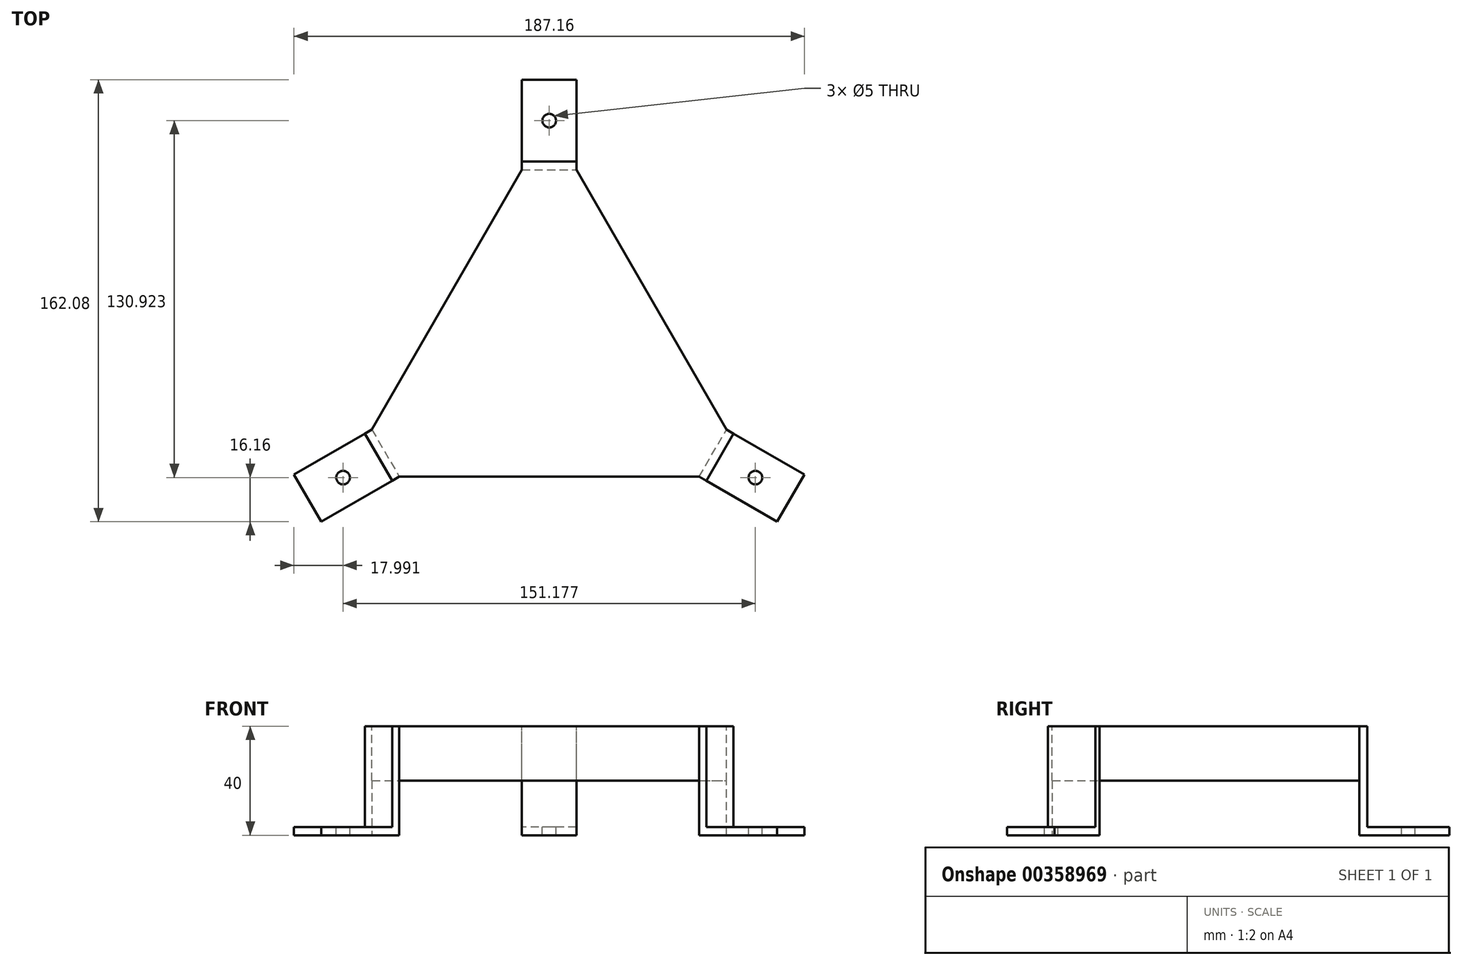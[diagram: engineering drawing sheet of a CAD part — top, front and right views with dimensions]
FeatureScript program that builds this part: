
annotation { "Feature Type Name" : "Feature", "Feature Type Description" : "" }
export const myFeature = defineFeature(function(context is Context, id is Id, definition is map)
    precondition{}
    {
        {
            var Q0;
            Q0=qCreatedBy(makeId("Top.planeOp"),FACE);
            var sketch = newSketch(context, id + "F0", { "sketchPlane" : qUnion([Q0])});
            skLineSegment(sketch, "E0", {"start": v(150, 0) * mm, "end": v(0, 0) * mm});
            skLineSegment(sketch, "E1", {"start": v(0, 0) * mm, "end": v(75, 129.9) * mm});
            skLineSegment(sketch, "E2", {"start": v(75, 129.9) * mm, "end": v(150, 0) * mm});
            skSolve(sketch);
        }
        {
            var Q0;
            Q0=makeQuery(id+"F0.imprint","IMPRINT",FACE,{"disambiguationData":[TD([[makeQuery(id+"F0.imprint","IMPRINT",EDGE,{"derivedFrom":sQuery(id+"F0.wireOp",EDGE,"E0")}),-1.0]])]});
            extrude(context, id + "F1", {"entities" : qUnion([Q0]), "depth" : 20 * mm});
        }
        {
            var Q0;
            Q0=makeQuery(id+"F1.opExtrude","CAP_FACE",FACE,{"disambiguationData":[OSD([sQuery(id+"F0.wireOp",EDGE,"E0"),sQuery(id+"F0.wireOp",EDGE,"E1"),sQuery(id+"F0.wireOp",EDGE,"E2")])],"isStart":false});
            var sketch = newSketch(context, id + "F2", { "sketchPlane" : qUnion([Q0])});
            skLineSegment(sketch, "E3", {"start": v(10, 17.32) * mm, "end": v(20, 0) * mm});
            skLineSegment(sketch, "E4", {"start": v(20, 0) * mm, "end": v(0, 0) * mm});
            skLineSegment(sketch, "E5", {"start": v(0, 0) * mm, "end": v(10, 17.32) * mm});
            skLineSegment(sketch, "E6", {"start": v(75, 129.9) * mm, "end": v(65, 112.58) * mm});
            skLineSegment(sketch, "E7", {"start": v(65, 112.58) * mm, "end": v(85, 112.58) * mm});
            skLineSegment(sketch, "E8", {"start": v(85, 112.58) * mm, "end": v(75, 129.9) * mm});
            skLineSegment(sketch, "E9", {"start": v(150, 0) * mm, "end": v(130, 0) * mm});
            skLineSegment(sketch, "E10", {"start": v(130, 0) * mm, "end": v(140, 17.32) * mm});
            skLineSegment(sketch, "E11", {"start": v(140, 17.32) * mm, "end": v(150, 0) * mm});
            skSolve(sketch);
        }
        {
            var Q0;
            Q0=makeQuery(id+"F2.imprint","IMPRINT",FACE,{"disambiguationData":[TD([[makeQuery(id+"F2.imprint","IMPRINT",EDGE,{"derivedFrom":sQuery(id+"F2.wireOp",EDGE,"E6")}),-1.0]])]});
            var Q1;
            Q1=makeQuery(id+"F2.imprint","IMPRINT",FACE,{"disambiguationData":[TD([[makeQuery(id+"F2.imprint","IMPRINT",EDGE,{"derivedFrom":sQuery(id+"F2.wireOp",EDGE,"E3")}),-1.0]])]});
            var Q2;
            Q2=makeQuery(id+"F2.imprint","IMPRINT",FACE,{"disambiguationData":[TD([[makeQuery(id+"F2.imprint","IMPRINT",EDGE,{"derivedFrom":sQuery(id+"F2.wireOp",EDGE,"E9")}),-1.0]])]});
            extrude(context, id + "F3", {"entities" : qUnion([Q0, Q1, Q2]), "operationType" : NewBodyOperationType.REMOVE, "endBound" : BoundingType.THROUGH_ALL, "oppositeDirection" : true, "depth" : 25.4 * mm});
        }
        {
            var Q0;
            Q0=makeQuery(id+"F3.boolean.opBoolean","COPY",FACE,{"derivedFrom":makeQuery(id+"F3.opExtrude","SWEPT_FACE",FACE,{"disambiguationData":[OSD([sQuery(id+"F2.wireOp",EDGE,"E10")])]})});
            var sketch = newSketch(context, id + "F4", { "sketchPlane" : qUnion([Q0])});
            skLineSegment(sketch, "E12", {"start": v(65, 20) * mm, "end": v(65, -20) * mm});
            skLineSegment(sketch, "E13", {"start": v(65, -20) * mm, "end": v(85, -20) * mm});
            skLineSegment(sketch, "E14", {"start": v(85, -20) * mm, "end": v(85, 20) * mm});
            skLineSegment(sketch, "E15", {"start": v(85, 20) * mm, "end": v(65, 20) * mm});
            skSolve(sketch);
        }
        {
            var Q0;
            {var subQ2=sQuery(id+"F4.wireOp",EDGE,"E13");Q0=makeQuery(id+"F4.imprint","IMPRINT",FACE,{"disambiguationData":[TD([[makeQuery(id+"F4.imprint","IMPRINT",EDGE,{"derivedFrom":subQ2}),1.0]])]});}
            var Q1;
            {var subQ0=sQuery(id+"F4.wireOp",EDGE,"E15");Q1=makeQuery(id+"F4.imprint","IMPRINT",FACE,{"disambiguationData":[TD([[makeQuery(id+"F4.imprint","IMPRINT",EDGE,{"derivedFrom":subQ0}),-1.0]])]});}
            extrude(context, id + "F5", {"entities" : qUnion([Q0, Q1]), "operationType" : NewBodyOperationType.ADD, "depth" : 3 * mm});
        }
        {
            var Q0;
            Q0=makeQuery(id+"F5.opExtrude","CAP_FACE",FACE,{"disambiguationData":[OSD([sQuery(id+"F4.wireOp",EDGE,"E12"),sQuery(id+"F4.wireOp",EDGE,"E13"),sQuery(id+"F4.wireOp",EDGE,"E14"),sQuery(id+"F4.wireOp",EDGE,"E15")])],"isStart":false});
            var sketch = newSketch(context, id + "F6", { "sketchPlane" : qUnion([Q0])});
            skLineSegment(sketch, "E16.bottom", {"start": v(65, -20) * mm, "end": v(85, -20) * mm});
            skLineSegment(sketch, "E16.top", {"start": v(65, -17) * mm, "end": v(85, -17) * mm});
            skLineSegment(sketch, "E16.left", {"start": v(65, -20) * mm, "end": v(65, -17) * mm});
            skLineSegment(sketch, "E16.right", {"start": v(85, -20) * mm, "end": v(85, -17) * mm});
            skSolve(sketch);
        }
        {
            var Q0;
            Q0=makeQuery(id+"F6.imprint","IMPRINT",FACE,{"disambiguationData":[TD([[makeQuery(id+"F6.imprint","IMPRINT",EDGE,{"derivedFrom":sQuery(id+"F6.wireOp",EDGE,"E16.bottom")}),1.0]])]});
            extrude(context, id + "F7", {"entities" : qUnion([Q0]), "operationType" : NewBodyOperationType.ADD, "depth" : 30 * mm});
        }
        {
            var Q0;
            Q0=makeQuery(id+"F7.opExtrude","SWEPT_FACE",FACE,{"disambiguationData":[OSD([sQuery(id+"F6.wireOp",EDGE,"E16.top")])]});
            var sketch = newSketch(context, id + "F8", { "sketchPlane" : qUnion([Q0])});
            skCircle(sketch, "E17", {"center": v(150.59, -0.34) * mm, "radius": 2.5 * mm});
            skSolve(sketch);
        }
        {
            var Q0;
            Q0=makeQuery(id+"F8.imprint","IMPRINT",FACE,{"disambiguationData":[TD([[makeQuery(id+"F8.imprint","IMPRINT",EDGE,{"derivedFrom":sQuery(id+"F8.wireOp",EDGE,"E17")}),1.0]])]});
            extrude(context, id + "F9", {"entities" : qUnion([Q0]), "operationType" : NewBodyOperationType.REMOVE, "endBound" : BoundingType.THROUGH_ALL, "oppositeDirection" : true, "depth" : 25.4 * mm});
        }
        {
            var Q0;
            Q0=makeQuery(id+"F3.boolean.opBoolean","COPY",FACE,{"derivedFrom":makeQuery(id+"F3.opExtrude","SWEPT_FACE",FACE,{"disambiguationData":[OSD([sQuery(id+"F2.wireOp",EDGE,"E7")])]})});
            var sketch = newSketch(context, id + "F10", { "sketchPlane" : qUnion([Q0])});
            skLineSegment(sketch, "E18.bottom", {"start": v(-85, 20) * mm, "end": v(-65, 20) * mm});
            skLineSegment(sketch, "E18.top", {"start": v(-85, -20) * mm, "end": v(-65, -20) * mm});
            skLineSegment(sketch, "E18.left", {"start": v(-85, 20) * mm, "end": v(-85, -20) * mm});
            skLineSegment(sketch, "E18.right", {"start": v(-65, 20) * mm, "end": v(-65, -20) * mm});
            skSolve(sketch);
        }
        {
            var Q0;
            {var subQ0=sQuery(id+"F10.wireOp",EDGE,"E18.bottom");Q0=makeQuery(id+"F10.imprint","IMPRINT",FACE,{"disambiguationData":[TD([[makeQuery(id+"F10.imprint","IMPRINT",EDGE,{"derivedFrom":subQ0}),1.0]])]});}
            var Q1;
            {var subQ0=sQuery(id+"F10.wireOp",EDGE,"E18.top");Q1=makeQuery(id+"F10.imprint","IMPRINT",FACE,{"disambiguationData":[TD([[makeQuery(id+"F10.imprint","IMPRINT",EDGE,{"derivedFrom":subQ0}),1.0]])]});}
            extrude(context, id + "F11", {"entities" : qUnion([Q0, Q1]), "operationType" : NewBodyOperationType.ADD, "depth" : 3 * mm});
        }
        {
            var Q0;
            Q0=makeQuery(id+"F11.opExtrude","CAP_FACE",FACE,{"disambiguationData":[OSD([sQuery(id+"F10.wireOp",EDGE,"E18.bottom"),sQuery(id+"F10.wireOp",EDGE,"E18.top"),sQuery(id+"F10.wireOp",EDGE,"E18.left"),sQuery(id+"F10.wireOp",EDGE,"E18.right")])],"isStart":false});
            var sketch = newSketch(context, id + "F12", { "sketchPlane" : qUnion([Q0])});
            skLineSegment(sketch, "E19.bottom", {"start": v(-85, -20) * mm, "end": v(-65, -20) * mm});
            skLineSegment(sketch, "E19.top", {"start": v(-85, -17) * mm, "end": v(-65, -17) * mm});
            skLineSegment(sketch, "E19.left", {"start": v(-85, -20) * mm, "end": v(-85, -17) * mm});
            skLineSegment(sketch, "E19.right", {"start": v(-65, -20) * mm, "end": v(-65, -17) * mm});
            skSolve(sketch);
        }
        {
            var Q0;
            Q0=makeQuery(id+"F12.imprint","IMPRINT",FACE,{"disambiguationData":[TD([[makeQuery(id+"F12.imprint","IMPRINT",EDGE,{"derivedFrom":sQuery(id+"F12.wireOp",EDGE,"E19.bottom")}),1.0]])]});
            extrude(context, id + "F13", {"entities" : qUnion([Q0]), "operationType" : NewBodyOperationType.ADD, "depth" : 30 * mm});
        }
        {
            var Q0;
            Q0=makeQuery(id+"F13.opExtrude","SWEPT_FACE",FACE,{"disambiguationData":[OSD([sQuery(id+"F12.wireOp",EDGE,"E19.top")])]});
            var sketch = newSketch(context, id + "F14", { "sketchPlane" : qUnion([Q0])});
            skCircle(sketch, "E20", {"center": v(75, 130.58) * mm, "radius": 2.5 * mm});
            skSolve(sketch);
        }
        {
            var Q0;
            Q0=makeQuery(id+"F14.imprint","IMPRINT",FACE,{"disambiguationData":[TD([[makeQuery(id+"F14.imprint","IMPRINT",EDGE,{"derivedFrom":sQuery(id+"F14.wireOp",EDGE,"E20")}),1.0]])]});
            extrude(context, id + "F15", {"entities" : qUnion([Q0]), "operationType" : NewBodyOperationType.REMOVE, "endBound" : BoundingType.THROUGH_ALL, "oppositeDirection" : true, "depth" : 25.4 * mm});
        }
        {
            var Q0;
            Q0=makeQuery(id+"F3.boolean.opBoolean","COPY",FACE,{"derivedFrom":makeQuery(id+"F3.opExtrude","SWEPT_FACE",FACE,{"disambiguationData":[OSD([sQuery(id+"F2.wireOp",EDGE,"E3")])]})});
            var sketch = newSketch(context, id + "F16", { "sketchPlane" : qUnion([Q0])});
            skLineSegment(sketch, "E21.bottom", {"start": v(-10, 20) * mm, "end": v(10, 20) * mm});
            skLineSegment(sketch, "E21.top", {"start": v(-10, -20) * mm, "end": v(10, -20) * mm});
            skLineSegment(sketch, "E21.left", {"start": v(-10, 20) * mm, "end": v(-10, -20) * mm});
            skLineSegment(sketch, "E21.right", {"start": v(10, 20) * mm, "end": v(10, -20) * mm});
            skSolve(sketch);
        }
        {
            var Q0;
            {var subQ0=sQuery(id+"F16.wireOp",EDGE,"E21.top");Q0=makeQuery(id+"F16.imprint","IMPRINT",FACE,{"disambiguationData":[TD([[makeQuery(id+"F16.imprint","IMPRINT",EDGE,{"derivedFrom":subQ0}),1.0]])]});}
            var Q1;
            {var subQ0=sQuery(id+"F16.wireOp",EDGE,"E21.bottom");Q1=makeQuery(id+"F16.imprint","IMPRINT",FACE,{"disambiguationData":[TD([[makeQuery(id+"F16.imprint","IMPRINT",EDGE,{"derivedFrom":subQ0}),-1.0]])]});}
            extrude(context, id + "F17", {"entities" : qUnion([Q0, Q1]), "operationType" : NewBodyOperationType.ADD, "depth" : 3 * mm});
        }
        {
            var Q0;
            Q0=makeQuery(id+"F17.opExtrude","CAP_FACE",FACE,{"disambiguationData":[OSD([sQuery(id+"F16.wireOp",EDGE,"E21.bottom"),sQuery(id+"F16.wireOp",EDGE,"E21.top"),sQuery(id+"F16.wireOp",EDGE,"E21.left"),sQuery(id+"F16.wireOp",EDGE,"E21.right")])],"isStart":false});
            var sketch = newSketch(context, id + "F18", { "sketchPlane" : qUnion([Q0])});
            skLineSegment(sketch, "E22.bottom", {"start": v(-10, -20) * mm, "end": v(10, -20) * mm});
            skLineSegment(sketch, "E22.top", {"start": v(-10, -17) * mm, "end": v(10, -17) * mm});
            skLineSegment(sketch, "E22.left", {"start": v(-10, -20) * mm, "end": v(-10, -17) * mm});
            skLineSegment(sketch, "E22.right", {"start": v(10, -20) * mm, "end": v(10, -17) * mm});
            skSolve(sketch);
        }
        {
            var Q0;
            Q0 = qSketchRegion(id + "F18", true);
            extrude(context, id + "F19", {"entities" : qUnion([Q0]), "operationType" : NewBodyOperationType.ADD, "depth" : 30 * mm});
        }
        {
            var Q0;
            Q0=makeQuery(id+"F19.opExtrude","SWEPT_FACE",FACE,{"disambiguationData":[OSD([sQuery(id+"F18.wireOp",EDGE,"E22.top")])]});
            var sketch = newSketch(context, id + "F20", { "sketchPlane" : qUnion([Q0])});
            skCircle(sketch, "E23", {"center": v(-0.59, -0.34) * mm, "radius": 2.5 * mm});
            skSolve(sketch);
        }
        {
            var Q0;
            Q0 = qSketchRegion(id + "F20", true);
            extrude(context, id + "F21", {"entities" : qUnion([Q0]), "operationType" : NewBodyOperationType.REMOVE, "endBound" : BoundingType.THROUGH_ALL, "oppositeDirection" : true, "depth" : 25.4 * mm});
        }
    });
